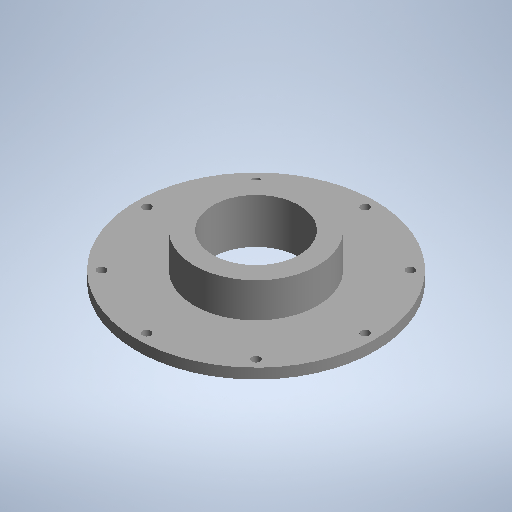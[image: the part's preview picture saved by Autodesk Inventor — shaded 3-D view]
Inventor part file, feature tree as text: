
AUTODESK INVENTOR PART (.ipt)
format: ipt  version: 2025 (Build 290162010, 162A)  size: 282,624 bytes
history: native  units: mm (DEFAULTED — no unit token found)
features: sketch x2, revolve x1, hole x1, pattern_circular x1, other x1
ambient origin geometry x8: Origin, YZ Plane, XZ Plane, XY Plane, X Axis, Y Axis, Z Axis, Center Point
bodies: Solid1 (feature_tree)
feature tree (6):
  revolve  "Revolution1"  [1 undecoded]
  hole  "Hole1"  [1 undecoded]
  pattern_circular  "Circular Pattern1"  [2 undecoded]
  sketch  "Sketch2"  dims[d1=70.0mm d2=119.0mm]
  sketch  "Sketch3"  dims[d3=29.0mm d4=134.0mm d5=16.0mm d6=90.0deg d7=340.0mm d9=13.0mm d10=6.0mm d11=4.0mm d12=2.0mm d13=90.0deg d14=8.0mm d15=20.594885mm d16=80.0mm d17=360.0deg]
  other  "Definition1"
note: 4 required parameter values undecoded (feature->parameter linkage not recoverable at this tier; creation-order binding heuristic only, values carry confidence <= 0.55)